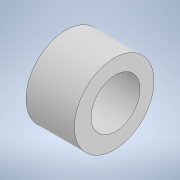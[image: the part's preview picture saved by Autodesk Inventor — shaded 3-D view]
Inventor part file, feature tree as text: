
AUTODESK INVENTOR PART (.ipt)
format: ipt  version: 2021 (Build 250183000, 183)  size: 100,864 bytes
history: native  units: mm
features: extrude x1, sketch x1
ambient origin geometry x8: Origin, YZ Plane, XZ Plane, XY Plane, X Axis, Y Axis, Z Axis, Center Point
bodies: Solid1 (feature_tree)
feature tree (2):
  extrude  "Extrusion1"  Depth=15.8mm
  sketch  "Sketch1"  dims[d0=26.0mm d1=16.0mm d2=15.8mm d3=0.0mm d4=0.5mm d5=0.872665mm]
